# Revit family: LQ4105551_Ducha Monocontrol Liquid Mate Black
name_source: partatom
category: Plumbing Fixtures
units: mm (PartAtom-declared; Revit-internal decimal feet)

## family parameters
Always vertical = Yes
Cut with Voids When Loaded = No
Host = Wall
OmniClass Number = 23.31.15.11
OmniClass Title = Bath Shower Units
Part Type = Normal
Room Calculation Point = No
Round Connector Dimension = Use Diameter
Shared = No

## types (1)
- Type 1
    Alto = 16.5 cm
    Altura ducha = 1800 mm  [stored 5.90551 ft]
    Altura mezclador = 900 mm  [stored 2.95276 ft]
    Ancho = 24.1 cm
    Capacidad de flujo = 9.50 l/m máximo a 80 psi
    Colección = Liquid
    Consumo de agua = 9.5 lt
    Creado por = IDD
    Description = La línea de griferías, duchas y accesorios Liquid se inspira en la tensión superficial del agua y en cómo esta crea formas armoniosas adaptándose al ambiente. Resistente a la corrosión, pelado y decoloración por agua. ¡Adquiérela ahora!
    Dimensión de la regadera = 24.1
    Fecha de creación = 09/10/2020
    Forma = Redondo
    Garantía = 30 años en estructura
    Garantías de otros componentes = 5 años en acabados
    Incluye = Cuerpo mezclador, Regadera, Brazo de la regadera y escudo, Manijas
    Largo = 41.5 cm
    Longitud del brazo = 41.5
    Línea = Liquid
    Material = Corona_Mate_Black
    Materiales = Polímero de alta ingeniería, Metal
    Model = LQ4105551
    Productos compatibles = Desviadores para ducha, Teleduchas, Accesorios individuales, Kits de accesorios para baño
    Rango de presión de agua = Entre 20 y 125 psi
    Resistencia = Resistente a la corrosión pelado y decoloración por agua
    Tecnologías = EcoStream
    Temperatura de uso = Entre 5˚C y 71˚C
    Tipo de chorro = Tipo lluvia
    Tipo de grifería = Monocontrol
    Tipo de manija/accionamiento = Palanca
    Tipo de regadera = Con funciones, Regadera con brazo
    Tipo mezclador = Monocontrol
    URL = https://corona.co
    Uso = Residencial

note: [stored X ft] marks values corroborated as IEEE doubles in the binary element streams (Revit-internal decimal feet)

## geometry (parser evidence)
native form markers: Sweep x11
no freeform markers — native parametric forms only
